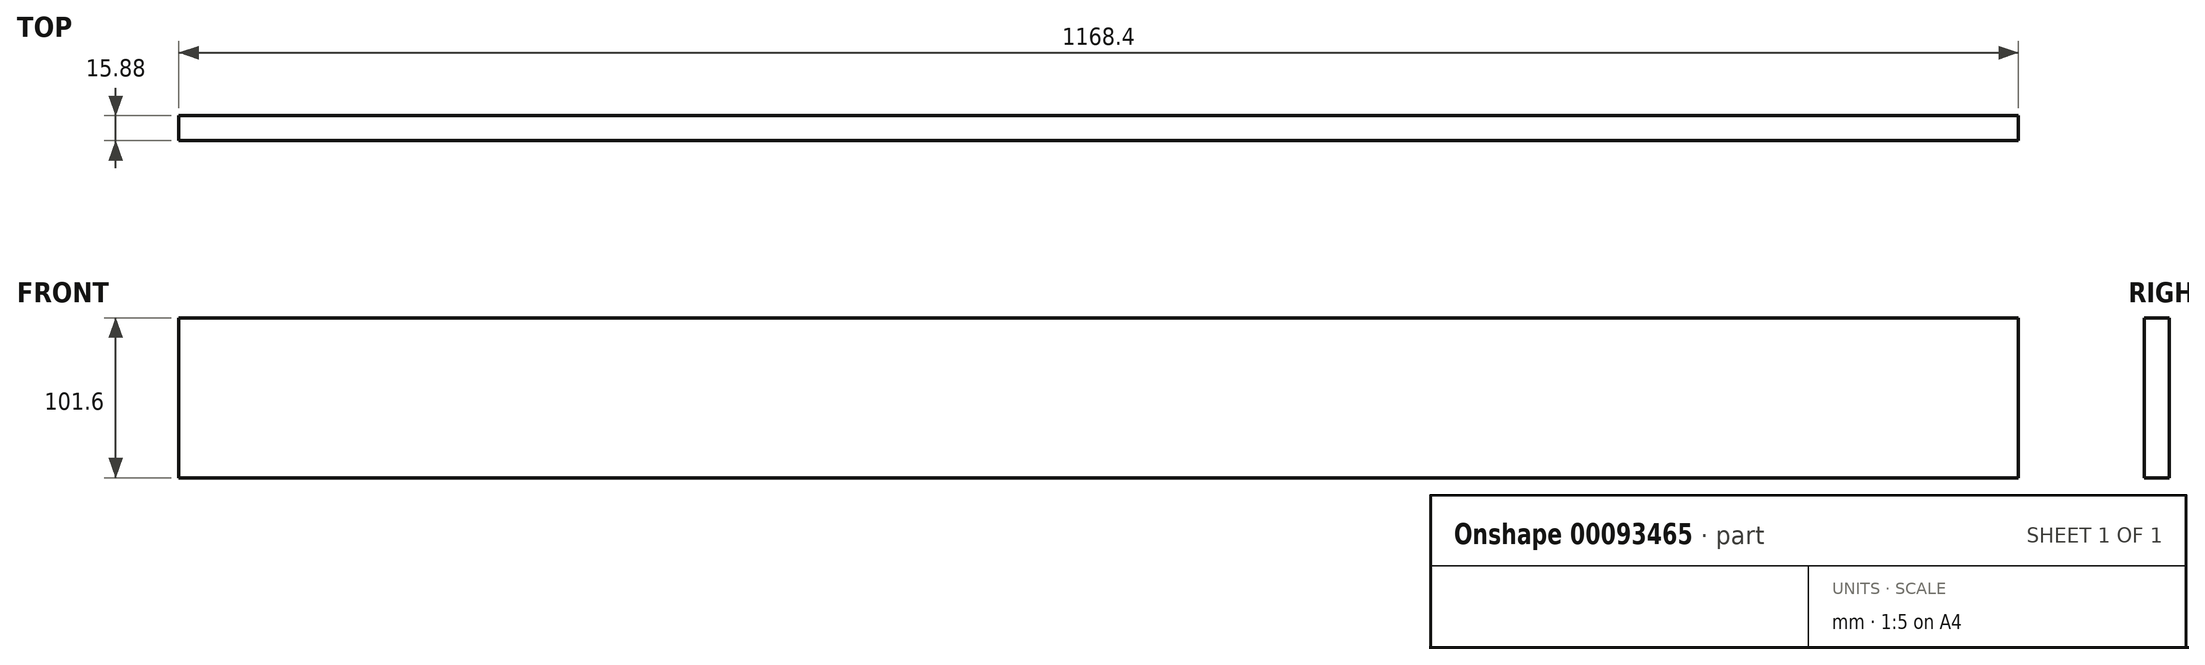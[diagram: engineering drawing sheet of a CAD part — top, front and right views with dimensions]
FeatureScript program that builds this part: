
annotation { "Feature Type Name" : "Feature", "Feature Type Description" : "" }
export const myFeature = defineFeature(function(context is Context, id is Id, definition is map)
    precondition{}
    {
        {
            var Q0;
            Q0=qCreatedBy(makeId("Top.planeOp"),FACE);
            var sketch = newSketch(context, id + "F0", { "sketchPlane" : qUnion([Q0])});
            skLineSegment(sketch, "E0.bottom", {"start": v(0, 0) * mm, "end": v(1168.4, 0) * mm});
            skLineSegment(sketch, "E0.top", {"start": v(0, 15.87) * mm, "end": v(1168.4, 15.87) * mm});
            skLineSegment(sketch, "E0.left", {"start": v(0, 0) * mm, "end": v(0, 15.87) * mm});
            skLineSegment(sketch, "E0.right", {"start": v(1168.4, 0) * mm, "end": v(1168.4, 15.87) * mm});
            skLineSegment(sketch, "E1.left", {"start": v(0, 441.32) * mm, "end": v(0, 457.2) * mm});
            skSolve(sketch);
        }
        {
            var Q0;
            Q0=makeQuery(id+"F0.imprint","IMPRINT",FACE,{"disambiguationData":[TD([[makeQuery(id+"F0.imprint","IMPRINT",EDGE,{"derivedFrom":sQuery(id+"F0.wireOp",EDGE,"E0.bottom")}),1.0]])]});
            var Q1;
            Q1=makeQuery(id+"F0.imprint","IMPRINT",FACE,{"disambiguationData":[TD([[makeQuery(id+"F0.imprint","IMPRINT",EDGE,{"derivedFrom":sQuery(id+"F0.wireOp",EDGE,"9wdDWlY4-uwBQ-jMWS-QeVb-W8KJ1ayq2p0f.bottom")}),1.0]])]});
            var Q2;
            Q2=makeQuery(id+"F0.imprint","IMPRINT",FACE,{"disambiguationData":[TD([[makeQuery(id+"F0.imprint","IMPRINT",EDGE,{"derivedFrom":sQuery(id+"F0.wireOp",EDGE,"E1.top")}),-1.0]])]});
            var Q3;
            Q3=makeQuery(id+"F0.imprint","IMPRINT",FACE,{"disambiguationData":[TD([[makeQuery(id+"F0.imprint","IMPRINT",EDGE,{"derivedFrom":sQuery(id+"F0.wireOp",EDGE,"czM6cofy-jgst-gK3K-igN0-a2iaJrsULNze.bottom")}),-1.0]])]});
            extrude(context, id + "F1", {"entities" : qUnion([Q0, Q1, Q2, Q3]), "depth" : 101.6 * mm});
        }
    });
